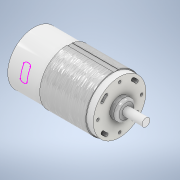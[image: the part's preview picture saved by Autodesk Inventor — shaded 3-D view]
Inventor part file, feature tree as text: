
AUTODESK INVENTOR PART (.ipt)
format: ipt  version: 2020 (Build 240168000, 168)  size: 229,376 bytes
history: native  units: in
note: dims shown in document units (in); Inventor stores cm internally (conversion verified against a paired STEP export)
features: sketch x9, extrude x8, fillet x1, other x1
ambient origin geometry x8: Origin, YZ Plane, XZ Plane, XY Plane, X Axis, Y Axis, Z Axis, Center Point
bodies: Solid1 (feature_tree)
feature tree (19):
  extrude  "Extrusion1"  Depth=2.5591in TaperAngle=0.0deg
  extrude  "Extrusion2"  Depth=0.1969in
  fillet  "Fillet1"  Radius=0.1969in
  extrude  "Extrusion3"  Depth=1.5748in TaperAngle=0.0deg
  extrude  "Extrusion4"  Depth=0.1575in
  extrude  "Extrusion5"  Depth=1.5748in TaperAngle=360.0deg
  extrude  "Extrusion6"  Depth=0.3937in TaperAngle=0.0deg
  sketch  "3D Sketch1"
  extrude  "Extrusion7"  Depth=0.7874in TaperAngle=0.0deg
  extrude  "Extrusion8"  Depth=0.0344in
  sketch  "Sketch1"  dims[d0=1.5748in d1=2.5591in d2=0.0in]
  sketch  "Sketch2"  dims[d3=0.5906in d4=0.2362in d5=0.1969in d6=0.0in]
  sketch  "Sketch3"  dims[d7=0.0787in d8=1.5748in d9=0.0in]
  sketch  "Sketch4"  dims[d10=0.1969in d11=0.0in d12=0.1575in]
  sketch  "Sketch5"  dims[d13=0.0in d14=0.0in d15=1.5748in d17=360.0deg]
  sketch  "Sketch6"  dims[d19=1.5748in d21=360.0deg d23=0.3937in d24=0.0in]
  other  "Project to Surface1"
  sketch  "Sketch8"  dims[d28=0.0787in d29=0.0in d30=0.7874in d31=0.0in]
  sketch  "Sketch9"  dims[d32=0.0197in d33=0.0344in]
